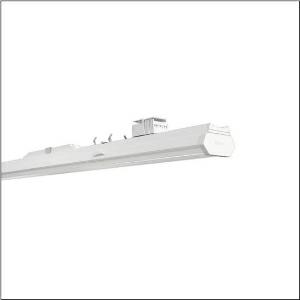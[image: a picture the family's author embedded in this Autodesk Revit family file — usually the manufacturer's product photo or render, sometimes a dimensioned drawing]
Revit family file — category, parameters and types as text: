
# Revit family: licross_r__11_protected_ho_51tp13mn4gxs_4b4b
name_source: partatom
category: Lighting Fixtures
units: mm (PartAtom-declared; Revit-internal decimal feet)

## family parameters
Cut with Voids When Loaded = No
Host = Face
Light Source = No
Part Type = Normal
Room Calculation Point = No
Round Connector Dimension = Use Diameter
Shared = No

## types (1)
- --- (1 x LED, 16110 lm, 87.4 W, 4000K)
    Apparent Load = 87 VA
    CIE Flux Codes = 89 96 99 100 99
    Color Rendering = 80
    Color Temperature = 4000K
    Default Elevation = 1800 mm
    Description = Licross® 11 Protected HO, luminaire insert, of sheet steel, galvanised, coil coated, white, length: 1.500mm, width: 90mm, height: 101mm, LED rated luminous flux: 16.110lm, light colour: 840, control gear: ON/OFF Multilumen, with plug, 3-pole, with phase selection, mains connection: 220..240V, AC, 50/60Hz, rated input power: 87W, internal wiring halogen-free, primary light control with lens, of plastic, primary optical cover: cover, of PMMA, light emission: direct distribution, primary light characteristic: symmetric, protection rating (complete): IP64, insulation class (complete): insulation class I (protective earthing), certification: CE, ENEC, VDE, UKCA, protection symbol: D if used in an environment with conductive dust loads with corresponding accessories, impact resistance: IK06, permissible ambient temperature for indoor applications: -35..+35°C, corresponds to IFS (International Featured Standards) requirements for safety and quality in the food industry, reducing of maximum allowable ambient temperature of 5°C with ceiling mounting, LABS conformity tested according to VDMA 24364:2018-05, packaging unit: 1 piece
    Height = 92 mm
    Lamp = 1 x LED
    Lamp Light Flux = 16110 lm
    Lamp Power = 87.4 W
    Lamp count = 1
    Length = 1500 mm
    Luminous efficacy = 184 lm/W
    Manufacturer = Siteco
    ModVariant = No
    Model = 51TP13MN4GXS
    Mounting Place = Ceiling
    Mounting Type = Pendant
    Number of Poles = 1
    OnlyDefault = Yes
    Power Factor = 1
    Product Name = Licross® 11 Protected HO
    Product group = luminaire insert | ceiling pendant
    ProductGroupID = 902
    Protection Class = Protection class I
    Protection Degree = IP 64
    RLX_Detail_Level = 1
    RLX_Emergency_Light_Flux = 0 lm
    RLX_Emergency_Type = 0
    RLX_Emergency_Type_DB = No
    RlxData = <blob elided: 21969 chars, md5=295abe14>
    Socket = socket
    Standby Power = 0 W
    System Light Flux = 16110 lm
    System Power = 87 W
    Type Comments = factory setting: luminous flux: 100 % | (A | C | E) | 203 mA
    Type Image = l_1256148.jpg
    URL = http://relux.com
    VarID = @adj_107225
    Voltage = 0 V
    Weight = 0.00 kg
    Width = 88 mm

## geometry (parser evidence)
native form markers: Blend x4, Sweep x9
no freeform markers — native parametric forms only
